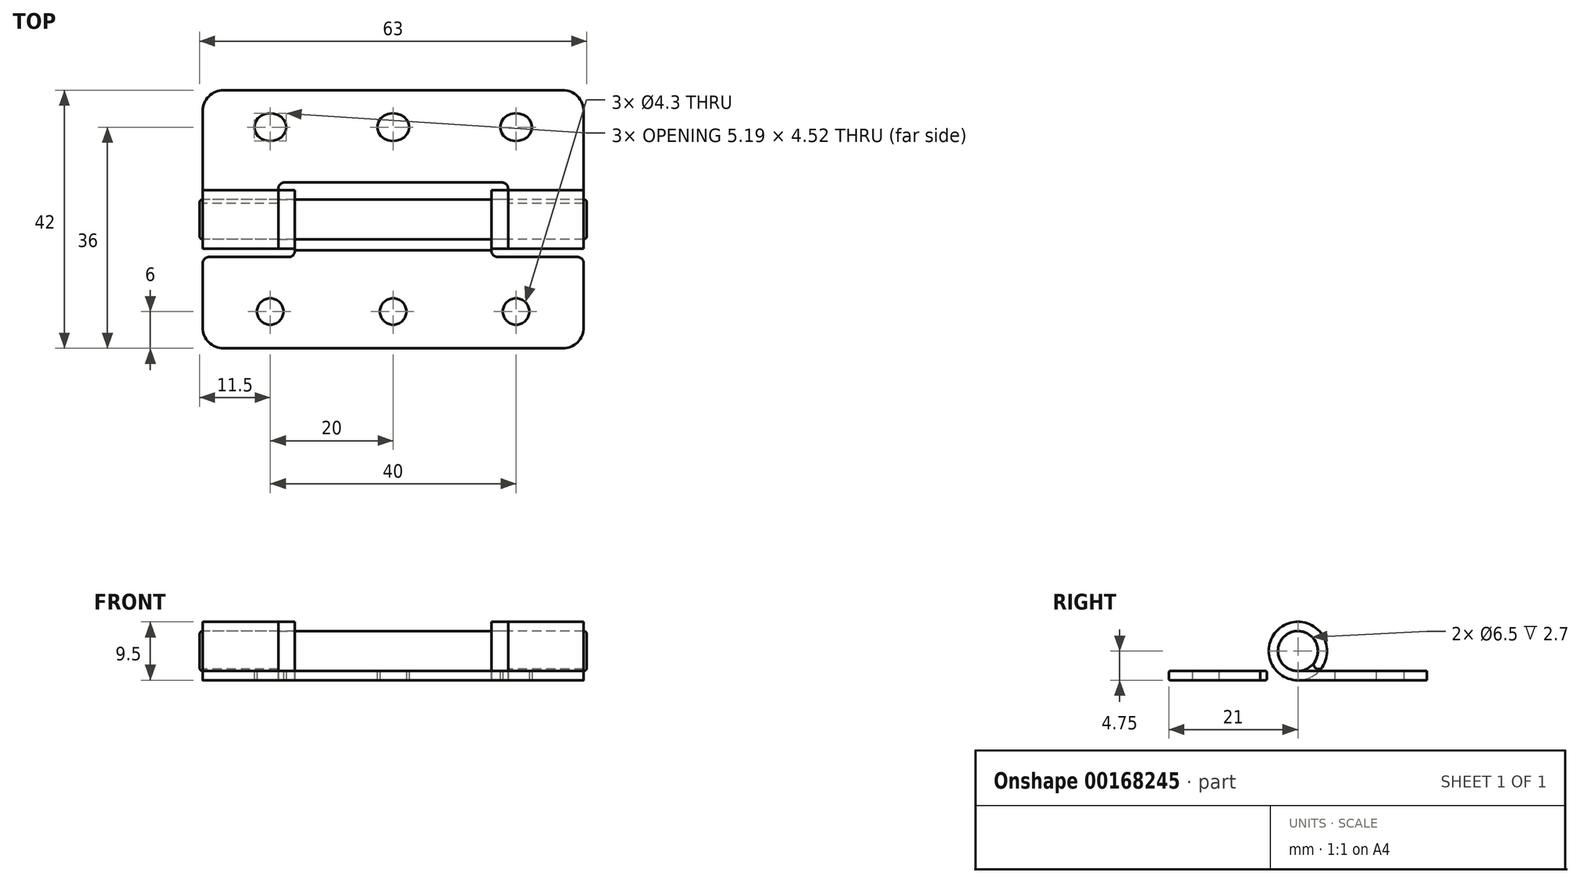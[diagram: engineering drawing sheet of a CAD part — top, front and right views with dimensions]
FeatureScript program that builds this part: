
annotation { "Feature Type Name" : "Feature", "Feature Type Description" : "" }
export const myFeature = defineFeature(function(context is Context, id is Id, definition is map)
    precondition{}
    {
        {
            var Q0;
            Q0=qCreatedBy(makeId("Top.planeOp"),FACE);
            var sketch = newSketch(context, id + "F0", { "sketchPlane" : qUnion([Q0])});
            skPoint(sketch, "E0.middle", {"position": v(0, 0) * mm});
            skPoint(sketch, "E1.startSnap0", {"position": v(-31.58, 13.48) * mm});
            skPoint(sketch, "E1.endSnap0", {"position": v(31.54, 13.48) * mm});
            skSolve(sketch);
        }
        {
            var Q0;
            Q0=qCreatedBy(makeId("Top.planeOp"),FACE);
            var sketch = newSketch(context, id + "F1", { "sketchPlane" : qUnion([Q0])});
            skLineSegment(sketch, "E2", {"start": v(-31, 0) * mm, "end": v(31, 0) * mm, "construction": true});
            skLineSegment(sketch, "E3", {"start": v(0, 27) * mm, "end": v(0, -21) * mm, "construction": true});
            skLineSegment(sketch, "E4", {"start": v(-20, 21) * mm, "end": v(-20, -21) * mm, "construction": true});
            skLineSegment(sketch, "E5", {"start": v(20, 21) * mm, "end": v(20, -21) * mm, "construction": true});
            skLineSegment(sketch, "E6", {"start": v(-31, 15) * mm, "end": v(31, 15) * mm, "construction": true});
            skLineSegment(sketch, "E7", {"start": v(-31, -15) * mm, "end": v(31, -15) * mm, "construction": true});
            skLineSegment(sketch, "E8", {"start": v(-31, 17.6) * mm, "end": v(-31, -4) * mm});
            skLineSegment(sketch, "E9", {"start": v(31, 17.6) * mm, "end": v(31, -4) * mm});
            skLineSegment(sketch, "E10", {"start": v(-18.7, 5) * mm, "end": v(-18.7, -4) * mm});
            skLineSegment(sketch, "E11", {"start": v(18.7, 5) * mm, "end": v(18.7, -4) * mm});
            skLineSegment(sketch, "E12", {"start": v(-27.6, 21) * mm, "end": v(27.6, 21) * mm});
            skLineSegment(sketch, "E13", {"start": v(-31, -4) * mm, "end": v(-18.7, -4) * mm});
            skLineSegment(sketch, "E14", {"start": v(-30, -6.14) * mm, "end": v(-17, -6.14) * mm});
            skLineSegment(sketch, "E15", {"start": v(-27.6, -21) * mm, "end": v(27.6, -21) * mm});
            skPoint(sketch, "E16.orphan", {"position": v(-39.8, 0) * mm});
            skLineSegment(sketch, "E17.trimOffspring", {"start": v(-17.7, 6) * mm, "end": v(17.7, 6) * mm});
            skLineSegment(sketch, "E18.trimOffspring", {"start": v(-16, 4) * mm, "end": v(-16, -5.14) * mm});
            skLineSegment(sketch, "E19.trimOffspring", {"start": v(16, 4) * mm, "end": v(16, -5.14) * mm});
            skPoint(sketch, "E20.visualSharp", {"position": v(-31, 21) * mm});
            skArc(sketch, "E20.filletArc", {"start": v(-27.6, 21) * mm, "mid": v(-30, 20) * mm, "end": v(-31, 17.6) * mm});
            skPoint(sketch, "E21.visualSharp", {"position": v(-31, -21) * mm});
            skArc(sketch, "E21.filletArc", {"start": v(-31, -17.6) * mm, "mid": v(-30, -20) * mm, "end": v(-27.6, -21) * mm});
            skPoint(sketch, "E22.visualSharp", {"position": v(31, -21) * mm});
            skArc(sketch, "E22.filletArc", {"start": v(27.6, -21) * mm, "mid": v(30, -20) * mm, "end": v(31, -17.6) * mm});
            skPoint(sketch, "E23.visualSharp", {"position": v(31, 21) * mm});
            skArc(sketch, "E23.filletArc", {"start": v(31, 17.6) * mm, "mid": v(30, 20) * mm, "end": v(27.6, 21) * mm});
            skLineSegment(sketch, "E24.trimOffspring", {"start": v(-31, -7.14) * mm, "end": v(-31, -17.6) * mm});
            skLineSegment(sketch, "E25.trimOffspring", {"start": v(31, -7.14) * mm, "end": v(31, -17.6) * mm});
            skLineSegment(sketch, "E26.trimOffspring", {"start": v(18.7, -4) * mm, "end": v(31, -4) * mm});
            skLineSegment(sketch, "E27.trimOffspring", {"start": v(-16, 4) * mm, "end": v(16, 4) * mm});
            skCircle(sketch, "E28", {"center": v(-20, -15) * mm, "radius": 2.15 * mm});
            skCircle(sketch, "E29", {"center": v(0, -15) * mm, "radius": 2.15 * mm});
            skCircle(sketch, "E30", {"center": v(20, -15) * mm, "radius": 2.15 * mm});
            skPoint(sketch, "E31.visualSharp", {"position": v(-31, -6.14) * mm});
            skArc(sketch, "E31.filletArc", {"start": v(-30, -6.14) * mm, "mid": v(-30.7, -6.43) * mm, "end": v(-31, -7.14) * mm});
            skArc(sketch, "E32.filletArc", {"start": v(-17, -6.14) * mm, "mid": v(-16.3, -5.85) * mm, "end": v(-16, -5.14) * mm});
            skPoint(sketch, "E33.visualSharp", {"position": v(-18.7, 6) * mm});
            skArc(sketch, "E33.filletArc", {"start": v(-17.7, 6) * mm, "mid": v(-18.4, 5.7) * mm, "end": v(-18.7, 5) * mm});
            skPoint(sketch, "E34.visualSharp", {"position": v(18.7, 6) * mm});
            skArc(sketch, "E34.filletArc", {"start": v(18.7, 5) * mm, "mid": v(18.4, 5.7) * mm, "end": v(17.7, 6) * mm});
            skLineSegment(sketch, "E35", {"start": v(17, -6.14) * mm, "end": v(30, -6.14) * mm});
            skPoint(sketch, "E36.visualSharp", {"position": v(16, -6.14) * mm});
            skArc(sketch, "E36.filletArc", {"start": v(16, -5.14) * mm, "mid": v(16.3, -5.85) * mm, "end": v(17, -6.14) * mm});
            skPoint(sketch, "E37.visualSharp", {"position": v(31, -6.14) * mm});
            skArc(sketch, "E37.filletArc", {"start": v(31, -7.14) * mm, "mid": v(30.7, -6.43) * mm, "end": v(30, -6.14) * mm});
            skEllipse(sketch, "E38", {"center": v(-20, 15) * mm, "majorRadius": 2.6 * mm, "minorRadius": 2.26 * mm, "majorAxis": v(1, 0)});
            skEllipse(sketch, "E39", {"center": v(0, 15) * mm, "majorRadius": 2.6 * mm, "minorRadius": 2.26 * mm, "majorAxis": v(1, 0)});
            skEllipse(sketch, "E40", {"center": v(20, 15) * mm, "majorRadius": 2.6 * mm, "minorRadius": 2.26 * mm, "majorAxis": v(1, 0)});
            skLineSegment(sketch, "E41", {"start": v(-16, -4) * mm, "end": v(16, -4) * mm});
            skLineSegment(sketch, "E42", {"start": v(-16, 4) * mm, "end": v(-31, 4) * mm});
            skLineSegment(sketch, "E43", {"start": v(16, 4) * mm, "end": v(31, 4) * mm});
            skSolve(sketch);
        }
        {
            var Q0;
            Q0=makeQuery(id+"F1.imprint","IMPRINT",FACE,{"disambiguationData":[TD([[makeQuery(id+"F1.imprint","IMPRINT",EDGE,{"derivedFrom":sQuery(id+"F1.wireOp",EDGE,"E14")}),-1.0]])]});
            var Q1;
            Q1=makeQuery(id+"F1.imprint","IMPRINT",FACE,{"disambiguationData":[TD([[makeQuery(id+"F1.imprint","IMPRINT",EDGE,{"derivedFrom":sQuery(id+"F1.wireOp",EDGE,"E12")}),-1.0]])]});
            extrude(context, id + "F2", {"entities" : qUnion([Q0, Q1]), "depth" : 1.5 * mm});
        }
        {
            var Q0;
            Q0=qCreatedBy(makeId("Right.planeOp"),FACE);
            var sketch = newSketch(context, id + "F3", { "sketchPlane" : qUnion([Q0])});
            skArc(sketch, "E44", {"start": v(0, 1.5) * mm, "mid": v(1.08, 7.82) * mm, "end": v(-2.04, 2.22) * mm});
            skArc(sketch, "E45.0", {"start": v(0, 0) * mm, "mid": v(2.3, 8.9) * mm, "end": v(-4.02, 2.22) * mm});
            skLineSegment(sketch, "E46.0", {"start": v(-4, 1.5) * mm, "end": v(-5.14, 1.5) * mm});
            skLineSegment(sketch, "E47.0", {"start": v(0, 0) * mm, "end": v(-5.14, 0) * mm});
            skLineSegment(sketch, "E48", {"start": v(-4, 1.5) * mm, "end": v(0, 1.5) * mm});
            skLineSegment(sketch, "E49", {"start": v(-2.04, 2.22) * mm, "end": v(-4.02, 2.22) * mm});
            skPoint(sketch, "E50.orphan", {"position": v(20.98, 0) * mm});
            skLineSegment(sketch, "E51", {"start": v(-5.14, 1.5) * mm, "end": v(-5.14, 0) * mm});
            skPoint(sketch, "E52.orphan", {"position": v(-21.14, 0) * mm});
            skSolve(sketch);
        }
        {
            var Q0;
            Q0 = qSketchRegion(id + "F3", true);
            extrude(context, id + "F4", {"entities" : qUnion([Q0]), "operationType" : NewBodyOperationType.ADD, "endBound" : BoundingType.SYMMETRIC, "depth" : 32 * mm});
        }
        {
            var Q0;
            Q0=makeQuery(id+"F4.opExtrude","SWEPT_EDGE",EDGE,{"disambiguationData":[OSD([sQuery(id+"F3.wireOp",EDGE,"E44"),sQuery(id+"F3.wireOp",EDGE,"E49")])]});
            var Q1;
            Q1=makeQuery(id+"F4.opExtrude","SWEPT_EDGE",EDGE,{"disambiguationData":[OSD([sQuery(id+"F3.wireOp",EDGE,"E45.0"),sQuery(id+"F3.wireOp",EDGE,"E49")])]});
            fillet(context, id + "F5", {"entities" : qUnion([Q0, Q1]), "radius" : 1 * mm, "tangentPropagation" : true, "allowEdgeOverflow" : false});
        }
        {
            var Q0;
            Q0=qCreatedBy(makeId("Right.planeOp"),FACE);
            var sketch = newSketch(context, id + "F6", { "sketchPlane" : qUnion([Q0])});
            skArc(sketch, "E53.5", {"start": v(3.97, 2.14) * mm, "mid": v(0.04, 9.5) * mm, "end": v(-4.02, 2.22) * mm});
            skArc(sketch, "E53.6", {"start": v(2.72, 2.97) * mm, "mid": v(-0.5, 7.96) * mm, "end": v(-2.04, 2.22) * mm});
            skArc(sketch, "E54", {"start": v(2.72, 2.97) * mm, "mid": v(-1.54, 7.6) * mm, "end": v(0, 1.5) * mm});
            skArc(sketch, "E55", {"start": v(3.97, 2.14) * mm, "mid": v(-2.26, 8.93) * mm, "end": v(0, 0) * mm});
            skPoint(sketch, "E53.2.start.orphan", {"position": v(-2.04, 2.22) * mm});
            skPoint(sketch, "E53.3.start.orphan", {"position": v(0, 0) * mm});
            skPoint(sketch, "E53.0.end.orphan", {"position": v(0, 1.5) * mm});
            skLineSegment(sketch, "E56.0", {"start": v(4, 1.5) * mm, "end": v(4, 0) * mm});
            skLineSegment(sketch, "E57", {"start": v(4, 1.5) * mm, "end": v(0, 1.5) * mm});
            skLineSegment(sketch, "E58", {"start": v(4, 0) * mm, "end": v(0, 0) * mm});
            skArc(sketch, "E59", {"start": v(2.72, 2.97) * mm, "mid": v(2.93, 1.93) * mm, "end": v(3.97, 2.14) * mm});
            skSolve(sketch);
        }
        {
            var Q0;
            Q0 = qSketchRegion(id + "F6", true);
            extrude(context, id + "F7", {"entities" : qUnion([Q0]), "operationType" : NewBodyOperationType.ADD, "endBound" : BoundingType.SYMMETRIC, "depth" : 62 * mm});
        }
        {
            var Q0;
            Q0=qCreatedBy(makeId("Top.planeOp"),FACE);
            var sketch = newSketch(context, id + "F8", { "sketchPlane" : qUnion([Q0])});
            skLineSegment(sketch, "E60.bottom", {"start": v(18.7, -5.05) * mm, "end": v(-18.7, -5.05) * mm});
            skLineSegment(sketch, "E60.top", {"start": v(18.7, 5.05) * mm, "end": v(-18.7, 5.05) * mm});
            skLineSegment(sketch, "E60.left", {"start": v(18.7, -5.05) * mm, "end": v(18.7, 5.05) * mm});
            skLineSegment(sketch, "E60.right", {"start": v(-18.7, -5.05) * mm, "end": v(-18.7, 5.05) * mm});
            skPoint(sketch, "E60.middle", {"position": v(0, 0) * mm});
            skSolve(sketch);
        }
        {
            var Q0;
            Q0 = qSketchRegion(id + "F8", true);
            extrude(context, id + "F9", {"entities" : qUnion([Q0]), "operationType" : NewBodyOperationType.REMOVE, "depth" : 25 * mm});
        }
        {
            var Q0;
            Q0=qCreatedBy(makeId("Front.planeOp"),FACE);
            var sketch = newSketch(context, id + "F10", { "sketchPlane" : qUnion([Q0])});
            skLineSegment(sketch, "E61.0", {"start": v(-16, 3.77) * mm, "end": v(-16, 1.5) * mm});
            skLineSegment(sketch, "E62.0", {"start": v(16, 3.77) * mm, "end": v(16, 1.5) * mm});
            skLineSegment(sketch, "E63", {"start": v(0, 7.6) * mm, "end": v(0, 0) * mm, "construction": true});
            skLineSegment(sketch, "E64.left", {"start": v(5, 2.3) * mm, "end": v(5, 2.8) * mm});
            skLineSegment(sketch, "E64.right", {"start": v(-5, 2.3) * mm, "end": v(-5, 2.8) * mm});
            skPoint(sketch, "E64.middle", {"position": v(0, 3.8) * mm});
            skLineSegment(sketch, "E65", {"start": v(-16, 9.5) * mm, "end": v(16, 9.5) * mm});
            skLineSegment(sketch, "E66", {"start": v(-16, 3.77) * mm, "end": v(-5, 2.8) * mm});
            skLineSegment(sketch, "E67.MirrorCS", {"start": v(16, 3.77) * mm, "end": v(5, 2.8) * mm});
            skPoint(sketch, "E68.orphan", {"position": v(-5, 5.3) * mm});
            skPoint(sketch, "E69.orphan", {"position": v(5, 5.3) * mm});
            skPoint(sketch, "E70.orphan", {"position": v(16, 9.5) * mm});
            skPoint(sketch, "E71.orphan", {"position": v(-16, 9.5) * mm});
            skPoint(sketch, "E72.0.start.orphan", {"position": v(-16, 2.8) * mm});
            skPoint(sketch, "E73.trimOffspring.end.orphan", {"position": v(16, 2.8) * mm});
            skLineSegment(sketch, "E74.0", {"start": v(-16, 1.5) * mm, "end": v(-5, 1.5) * mm});
            skPoint(sketch, "E75.orphan", {"position": v(-27.6, 1.5) * mm});
            skPoint(sketch, "E76.orphan", {"position": v(-16, 0) * mm});
            skPoint(sketch, "E77.orphan", {"position": v(16, 0) * mm});
            skPoint(sketch, "E78.orphan", {"position": v(27.6, 1.5) * mm});
            skLineSegment(sketch, "E79", {"start": v(-5, 2.8) * mm, "end": v(-5, 1.5) * mm});
            skLineSegment(sketch, "E80", {"start": v(5, 2.8) * mm, "end": v(5, 1.5) * mm});
            skLineSegment(sketch, "E81.trimOffspring", {"start": v(5, 1.5) * mm, "end": v(16, 1.5) * mm});
            skSolve(sketch);
        }
        {
            var Q0;
            Q0 = qSketchRegion(id + "F10", true);
            extrude(context, id + "F11", {"entities" : qUnion([Q0]), "operationType" : NewBodyOperationType.REMOVE, "depth" : 25 * mm});
        }
        {
            var Q0;
            Q0=makeQuery(id+"F4.boolean.opBoolean","MERGE",FACE,{"derivedFrom":[makeQuery(id+"F2.opExtrude","SWEPT_FACE",FACE,{"disambiguationData":[OSD([sQuery(id+"F1.wireOp",EDGE,"E19.trimOffspring")])]}),makeQuery(id+"F4.opExtrude","CAP_FACE",FACE,{"disambiguationData":[OSD([sQuery(id+"F3.wireOp",EDGE,"E44"),sQuery(id+"F3.wireOp",EDGE,"E45.0"),sQuery(id+"F3.wireOp",EDGE,"E46.0"),sQuery(id+"F3.wireOp",EDGE,"E47.0"),sQuery(id+"F3.wireOp",EDGE,"E48"),sQuery(id+"F3.wireOp",EDGE,"E49"),sQuery(id+"F3.wireOp",EDGE,"E51")])],"isStart":false})]});
            cPlane(context, id + "F12", {"entities" : qUnion([Q0]), "cplaneType" : CPlaneType.OFFSET, "offset" : 1.35 * mm, "width" : 150 * mm, "height" : 150 * mm});
        }
        {
            var Q0;
            Q0=qCreatedBy(id+"F12.planeOp",FACE);
            var sketch = newSketch(context, id + "F13", { "sketchPlane" : qUnion([Q0])});
            skCircle(sketch, "E82", {"center": v(0, 4.75) * mm, "radius": 3.25 * mm});
            skLineSegment(sketch, "E83", {"start": v(0, 0) * mm, "end": v(0, 4.75) * mm, "construction": true});
            skCircle(sketch, "E84", {"center": v(0, 4.75) * mm, "radius": 4.75 * mm});
            skSolve(sketch);
        }
        {
            var Q0;
            Q0=makeQuery(id+"F13.imprint","IMPRINT",FACE,{"disambiguationData":[TD([[makeQuery(id+"F13.imprint","IMPRINT",EDGE,{"derivedFrom":sQuery(id+"F13.wireOp",EDGE,"E82")}),-1.0]])]});
            extrude(context, id + "F14", {"entities" : qUnion([Q0]), "endBound" : BoundingType.SYMMETRIC, "depth" : 2.7 * mm});
        }
        {
            var Q0;
            Q0=makeQuery(id+"F14.opExtrude","SWEPT_BODY",BODY,{"disambiguationData":[OSD([sQuery(id+"F13.wireOp",EDGE,"E82"),sQuery(id+"F13.wireOp",EDGE,"E84")])]});
            var Q1;
            Q1=qCreatedBy(makeId("Right.planeOp"),FACE);
            mirror(context, id + "F15", {"entities" : qUnion([Q0]), "mirrorPlane" : qUnion([Q1])});
        }
        {
            var Q0;
            Q0=qCreatedBy(makeId("Right.planeOp"),FACE);
            var sketch = newSketch(context, id + "F16", { "sketchPlane" : qUnion([Q0])});
            skCircle(sketch, "E85.0", {"center": v(0, 4.75) * mm, "radius": 3.25 * mm});
            skSolve(sketch);
        }
        {
            var Q0;
            Q0 = qSketchRegion(id + "F16", true);
            extrude(context, id + "F17", {"entities" : qUnion([Q0]), "endBound" : BoundingType.SYMMETRIC, "depth" : 63 * mm});
        }
        {
            var Q0;
            Q0=makeQuery(id+"F2.opExtrude","CAP_EDGE",EDGE,{"disambiguationData":[OSD([sQuery(id+"F1.wireOp",EDGE,"E12")])],"isStart":false});
            var Q1;
            Q1=makeQuery(id+"F2.opExtrude","CAP_EDGE",EDGE,{"disambiguationData":[OSD([sQuery(id+"F1.wireOp",EDGE,"E23.filletArc")])],"isStart":false});
            var Q2;
            Q2=makeQuery(id+"F7.boolean.opBoolean","MERGE",EDGE,{"derivedFrom":[makeQuery(id+"F2.opExtrude","CAP_EDGE",EDGE,{"disambiguationData":[OSD([sQuery(id+"F1.wireOp",EDGE,"E9")])],"isStart":false}),makeQuery(id+"F7.opExtrude","CAP_EDGE",EDGE,{"disambiguationData":[OSD([sQuery(id+"F6.wireOp",EDGE,"E57")])],"isStart":false})]});
            var Q3;
            Q3=makeQuery(id+"F7.boolean.opBoolean","MERGE",EDGE,{"derivedFrom":[makeQuery(id+"F2.opExtrude","CAP_EDGE",EDGE,{"disambiguationData":[OSD([sQuery(id+"F1.wireOp",EDGE,"E8")])],"isStart":false}),makeQuery(id+"F7.opExtrude","CAP_EDGE",EDGE,{"disambiguationData":[OSD([sQuery(id+"F6.wireOp",EDGE,"E57")])],"isStart":true})]});
            var Q4;
            Q4=makeQuery(id+"F2.opExtrude","CAP_EDGE",EDGE,{"disambiguationData":[OSD([sQuery(id+"F1.wireOp",EDGE,"E20.filletArc")])],"isStart":false});
            var Q5;
            Q5=makeQuery(id+"F2.opExtrude","CAP_EDGE",EDGE,{"disambiguationData":[OSD([sQuery(id+"F1.wireOp",EDGE,"E24.trimOffspring")])],"isStart":false});
            var Q6;
            Q6=makeQuery(id+"F2.opExtrude","CAP_EDGE",EDGE,{"disambiguationData":[OSD([sQuery(id+"F1.wireOp",EDGE,"E14")])],"isStart":false});
            var Q7;
            Q7=makeQuery(id+"F2.opExtrude","CAP_EDGE",EDGE,{"disambiguationData":[OSD([sQuery(id+"F1.wireOp",EDGE,"E31.filletArc")])],"isStart":false});
            var Q8;
            Q8=makeQuery(id+"F11.boolean.opBoolean","INTERSECT",EDGE,{"derivedFrom":[makeQuery(id+"F11.opExtrude","SWEPT_FACE",FACE,{"disambiguationData":[OSD([sQuery(id+"F10.wireOp",EDGE,"E74.0")])]}),makeQuery(id+"F11.opExtrude","SWEPT_FACE",FACE,{"disambiguationData":[OSD([sQuery(id+"F10.wireOp",EDGE,"E81.trimOffspring")])]})]});
            var Q9;
            Q9=makeQuery(id+"F2.opExtrude","CAP_EDGE",EDGE,{"disambiguationData":[OSD([sQuery(id+"F1.wireOp",EDGE,"E21.filletArc")])],"isStart":false});
            var Q10;
            Q10=makeQuery(id+"F2.opExtrude","CAP_EDGE",EDGE,{"disambiguationData":[OSD([sQuery(id+"F1.wireOp",EDGE,"E35")])],"isStart":false});
            var Q11;
            Q11=makeQuery(id+"F2.opExtrude","CAP_EDGE",EDGE,{"disambiguationData":[OSD([sQuery(id+"F1.wireOp",EDGE,"E37.filletArc")])],"isStart":false});
            var Q12;
            Q12=makeQuery(id+"F2.opExtrude","CAP_EDGE",EDGE,{"disambiguationData":[OSD([sQuery(id+"F1.wireOp",EDGE,"E25.trimOffspring")])],"isStart":false});
            var Q13;
            Q13=makeQuery(id+"F2.opExtrude","CAP_EDGE",EDGE,{"disambiguationData":[OSD([sQuery(id+"F1.wireOp",EDGE,"E22.filletArc")])],"isStart":false});
            var Q14;
            Q14=makeQuery(id+"F4.boolean.opBoolean","MERGE",FACE,{"derivedFrom":[makeQuery(id+"F2.opExtrude","CAP_FACE",FACE,{"disambiguationData":[OSD([sQuery(id+"F1.wireOp",EDGE,"E14"),sQuery(id+"F1.wireOp",EDGE,"E15"),sQuery(id+"F1.wireOp",EDGE,"E18.trimOffspring"),sQuery(id+"F1.wireOp",EDGE,"E19.trimOffspring"),sQuery(id+"F1.wireOp",EDGE,"E21.filletArc"),sQuery(id+"F1.wireOp",EDGE,"E22.filletArc"),sQuery(id+"F1.wireOp",EDGE,"E24.trimOffspring"),sQuery(id+"F1.wireOp",EDGE,"E25.trimOffspring"),sQuery(id+"F1.wireOp",EDGE,"E28"),sQuery(id+"F1.wireOp",EDGE,"E29"),sQuery(id+"F1.wireOp",EDGE,"E30"),sQuery(id+"F1.wireOp",EDGE,"E31.filletArc"),sQuery(id+"F1.wireOp",EDGE,"E32.filletArc"),sQuery(id+"F1.wireOp",EDGE,"E35"),sQuery(id+"F1.wireOp",EDGE,"E36.filletArc"),sQuery(id+"F1.wireOp",EDGE,"E37.filletArc"),sQuery(id+"F1.wireOp",EDGE,"E41")])],"isStart":true}),makeQuery(id+"F4.opExtrude","SWEPT_FACE",FACE,{"disambiguationData":[OSD([sQuery(id+"F3.wireOp",EDGE,"E47.0")])]})]});
            var Q15;
            Q15=makeQuery(id+"F7.boolean.opBoolean","MERGE",FACE,{"derivedFrom":[makeQuery(id+"F2.opExtrude","CAP_FACE",FACE,{"disambiguationData":[OSD([sQuery(id+"F1.wireOp",EDGE,"E8"),sQuery(id+"F1.wireOp",EDGE,"E9"),sQuery(id+"F1.wireOp",EDGE,"E10"),sQuery(id+"F1.wireOp",EDGE,"E11"),sQuery(id+"F1.wireOp",EDGE,"E12"),sQuery(id+"F1.wireOp",EDGE,"E17.trimOffspring"),sQuery(id+"F1.wireOp",EDGE,"E20.filletArc"),sQuery(id+"F1.wireOp",EDGE,"E23.filletArc"),sQuery(id+"F1.wireOp",EDGE,"E33.filletArc"),sQuery(id+"F1.wireOp",EDGE,"E34.filletArc"),sQuery(id+"F1.wireOp",EDGE,"E38"),sQuery(id+"F1.wireOp",EDGE,"E39"),sQuery(id+"F1.wireOp",EDGE,"E40"),sQuery(id+"F1.wireOp",EDGE,"E42"),sQuery(id+"F1.wireOp",EDGE,"E43")])],"isStart":true}),makeQuery(id+"F7.opExtrude","SWEPT_FACE",FACE,{"disambiguationData":[OSD([sQuery(id+"F6.wireOp",EDGE,"E58")])]})]});
            fillet(context, id + "F18", {"entities" : qUnion([Q0, Q1, Q2, Q3, Q4, Q5, Q6, Q7, Q8, Q9, Q10, Q11, Q12, Q13, Q14, Q15]), "radius" : 0.2 * mm, "tangentPropagation" : true, "allowEdgeOverflow" : false});
        }
        {
            var Q0;
            Q0=makeQuery(id+"F17.opExtrude","CAP_FACE",FACE,{"disambiguationData":[OSD([sQuery(id+"F16.wireOp",EDGE,"E85.0")])],"isStart":false});
            var Q1;
            Q1=makeQuery(id+"F17.opExtrude","CAP_FACE",FACE,{"disambiguationData":[OSD([sQuery(id+"F16.wireOp",EDGE,"E85.0")])],"isStart":true});
            fillet(context, id + "F19", {"entities" : qUnion([Q0, Q1]), "radius" : 0.5 * mm, "tangentPropagation" : true, "allowEdgeOverflow" : false});
        }
    });
